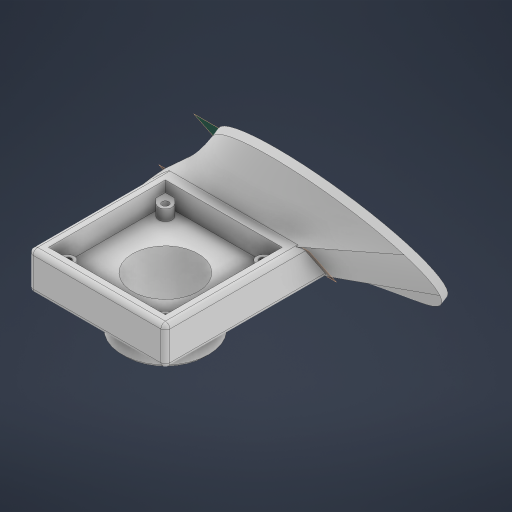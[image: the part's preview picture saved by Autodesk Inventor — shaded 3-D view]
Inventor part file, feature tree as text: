
AUTODESK INVENTOR PART (.ipt)
format: ipt  version: 2023 (Build 270158000, 158)  size: 486,400 bytes
history: native  units: in
note: dims shown in document units (in); Inventor stores cm internally (conversion verified against a paired STEP export)
features: sketch x9, extrude x6, hole x3, plane x2, fillet x2, chamfer x2, projected_geometry x2, other x2, loft x1
ambient origin geometry x8: Origin, YZ Plane, XZ Plane, XY Plane, X Axis, Y Axis, Z Axis, Center Point
bodies: Solid1 (feature_tree)
feature tree (29):
  extrude  "Extrusion1"  Depth=0.525in
  extrude  "Extrusion2"  Depth=0.3848in
  plane  "Work Plane1"
  extrude  "Extrusion3"  Depth=0.6in
  loft  "Loft1"
  extrude  "Extrusion4"  Depth=1.6in
  hole  "Hole1"  [1 undecoded]
  extrude  "Extrusion5"  Depth=0.1839in
  extrude  "Extrusion6"  Depth=0.15in TaperAngle=0.0deg
  hole  "Hole2"  [1 undecoded]
  plane  "Work Plane2"
  hole  "Hole3"  [1 undecoded]
  fillet  "Fillet1"  Radius=0.4466in
  chamfer  "Chamfer1"  Distance=0.4in
  fillet  "Fillet2"  Radius=0.65in
  chamfer  "Chamfer2"  Distance=0.0625in
  sketch  "Sketch1"  dims[d0=1.875in d1=0.525in]
  sketch  "Sketch2"  dims[d2=1.875in d3=0.0in d4=0.3848in]
  sketch  "Sketch3"  dims[d5=1.875in d6=0.0in d7=0.6in]
  sketch  "Sketch4"  dims[d9=2.875in d10=0.1in d11=0.0in]
  projected_geometry  "Projected Loop1"
  sketch  "Sketch5"  dims[d14=0.0in d15=90.0deg d16=1.6in]
  sketch  "Sketch6"  dims[d17=0.3in d18=0.0in]
  sketch  "Sketch7"  dims[d19=0.9in d20=0.75in d21=0.119in d22=0.25in d23=0.6871in d24=1.0in d25=0.8108in d26=1.1875in]
  projected_geometry  "Projected Loop2"
  sketch  "Sketch8"  dims[d27=0.5in d28=0.0in d29=0.1839in]
  sketch  "Sketch9"  dims[d30=1.3386in d31=0.15in d32=0.0in d33=0.094in d34=0.75in d35=0.251in d36=0.15in d37=0.6871in d38=1.0in d39=0.8108in d40=0.9792in d41=0.9792in d42=0.4466in d43=0.4in d44=0.65in d45=0.177in d46=0.75in d47=0.313in d48=0.45in d49=0.5635in d50=1.0in d51=0.8108in d52=0.0625in d53=0.05in d54=0.125in d55=45.0deg d56=0.0625in d61=0.02in d62=0.125in d63=45.0deg d64=2.75in d65=0.0in d66=90.0deg]
  other  "Edges2"
  other  "Edges3"
note: 3 required parameter values undecoded (feature->parameter linkage not recoverable at this tier; creation-order binding heuristic only, values carry confidence <= 0.55)
